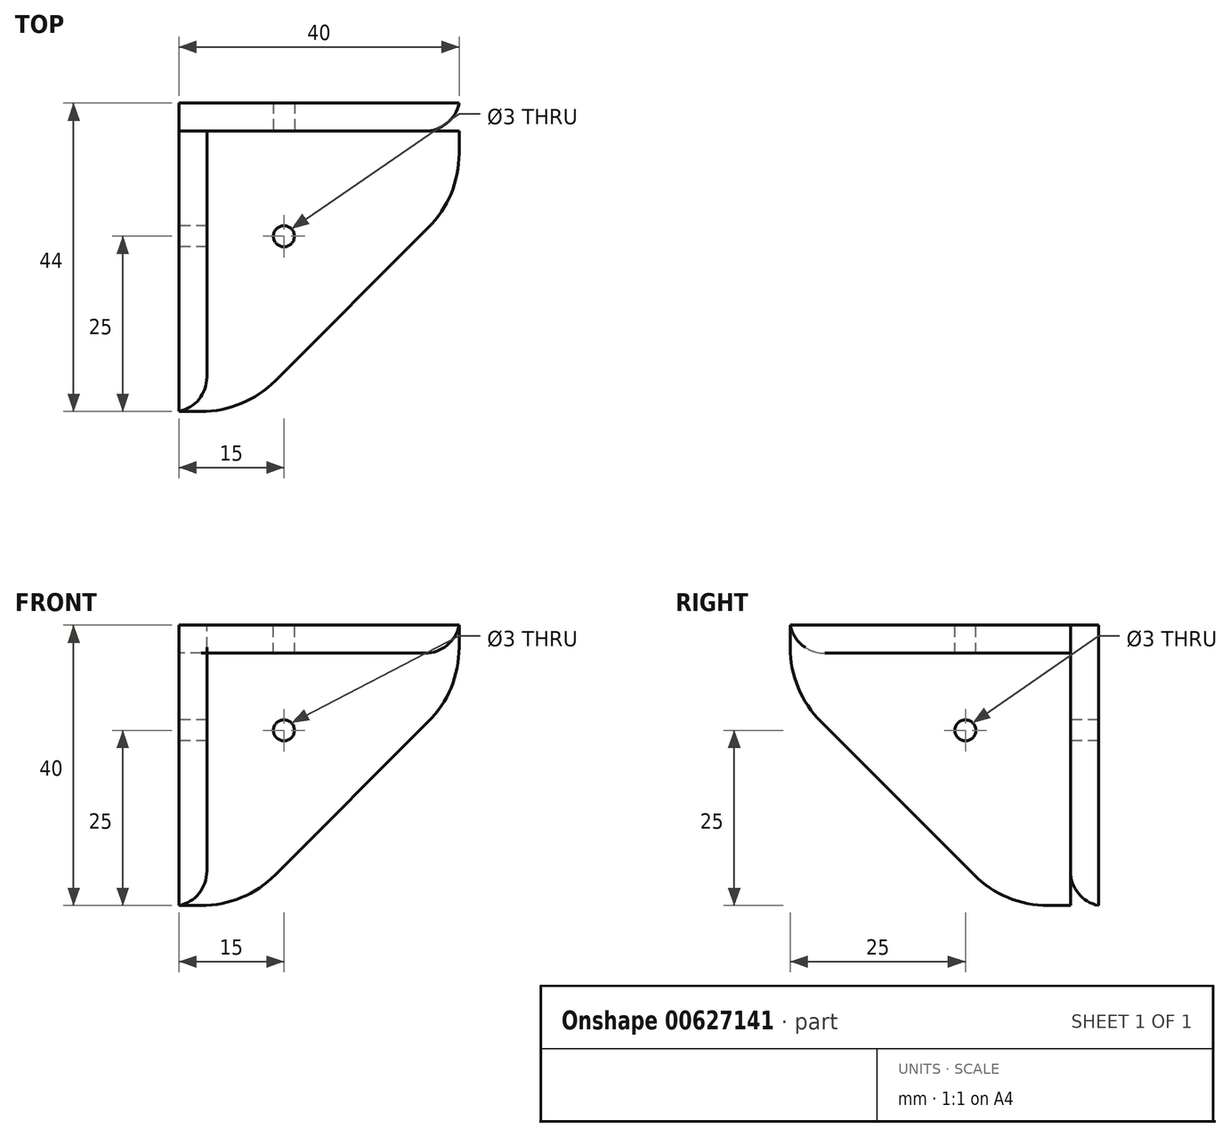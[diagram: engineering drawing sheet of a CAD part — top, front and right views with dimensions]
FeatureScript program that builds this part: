
annotation { "Feature Type Name" : "Feature", "Feature Type Description" : "" }
export const myFeature = defineFeature(function(context is Context, id is Id, definition is map)
    precondition{}
    {
        {
            var Q0;
            Q0=qCreatedBy(makeId("Front.planeOp"),FACE);
            var sketch = newSketch(context, id + "F0", { "sketchPlane" : qUnion([Q0])});
            skLineSegment(sketch, "E0.bottom", {"start": v(0, 0) * mm, "end": v(40, 0) * mm});
            skLineSegment(sketch, "E0.top", {"start": v(0, -40) * mm, "end": v(40, -40) * mm});
            skLineSegment(sketch, "E0.left", {"start": v(0, 0) * mm, "end": v(0, -40) * mm});
            skLineSegment(sketch, "E0.right", {"start": v(40, 0) * mm, "end": v(40, -40) * mm});
            skLineSegment(sketch, "E1", {"start": v(57.97, 8.58) * mm, "end": v(-37.76, -87.15) * mm});
            skPoint(sketch, "E2", {"position": v(0, -15) * mm});
            skPoint(sketch, "E3", {"position": v(15, 0) * mm});
            skCircle(sketch, "E4", {"center": v(15, -15) * mm, "radius": 1.5 * mm});
            skSolve(sketch);
        }
        {
            var Q0;
            {var subQ1=sQuery(id+"F0.wireOp",EDGE,"E0.bottom");Q0=makeQuery(id+"F0.imprint","IMPRINT",FACE,{"disambiguationData":[TD([[makeQuery(id+"F0.imprint","IMPRINT",EDGE,{"derivedFrom":subQ1}),-1.0]])]});}
            extrude(context, id + "F1", {"entities" : qUnion([Q0]), "oppositeDirection" : true, "depth" : 4 * mm, "offsetDistance" : 25 * mm});
        }
        {
            var Q0;
            Q0=makeQuery(id+"F1.opExtrude","SWEPT_EDGE",EDGE,{"disambiguationData":[OSD([sQuery(id+"F0.wireOp",EDGE,"E0.top"),sQuery(id+"F0.wireOp",EDGE,"E1")])]});
            var Q1;
            Q1=makeQuery(id+"F1.opExtrude","SWEPT_EDGE",EDGE,{"disambiguationData":[OSD([sQuery(id+"F0.wireOp",EDGE,"E0.right"),sQuery(id+"F0.wireOp",EDGE,"E1")])]});
            fillet(context, id + "F2", {"entities" : qUnion([Q0, Q1]), "radius" : 15 * mm, "tangentPropagation" : true, "allowEdgeOverflow" : false});
        }
        {
            var Q0;
            Q0=makeQuery(id+"F1.opExtrude","SWEPT_BODY",BODY,{"disambiguationData":[OSD([sQuery(id+"F0.wireOp",EDGE,"E0.bottom"),sQuery(id+"F0.wireOp",EDGE,"E0.top"),sQuery(id+"F0.wireOp",EDGE,"E0.left"),sQuery(id+"F0.wireOp",EDGE,"E0.right"),sQuery(id+"F0.wireOp",EDGE,"E1"),sQuery(id+"F0.wireOp",EDGE,"E4")])]});
            var Q1;
            Q1=makeQuery(id+"F1.opExtrude","CAP_EDGE",EDGE,{"disambiguationData":[OSD([sQuery(id+"F0.wireOp",EDGE,"E0.left")])],"isStart":true});
            transform(context, id + "F3", {"entities" : qUnion([Q0]), "transformType" : TransformType.ROTATION, "transformAxis" : qUnion([Q1]), "angle" : 90 * degree, "makeCopy" : true});
        }
        {
            var Q0;
            Q0=makeQuery(id+"F1.opExtrude","SWEPT_BODY",BODY,{"disambiguationData":[OSD([sQuery(id+"F0.wireOp",EDGE,"E0.bottom"),sQuery(id+"F0.wireOp",EDGE,"E0.top"),sQuery(id+"F0.wireOp",EDGE,"E0.left"),sQuery(id+"F0.wireOp",EDGE,"E0.right"),sQuery(id+"F0.wireOp",EDGE,"E1"),sQuery(id+"F0.wireOp",EDGE,"E4")])]});
            var Q1;
            Q1=makeQuery(id+"F1.opExtrude","CAP_EDGE",EDGE,{"disambiguationData":[OSD([sQuery(id+"F0.wireOp",EDGE,"E0.bottom")])],"isStart":true});
            transform(context, id + "F4", {"entities" : qUnion([Q0]), "transformType" : TransformType.ROTATION, "transformAxis" : qUnion([Q1]), "angle" : 270 * degree, "makeCopy" : true});
        }
        {
            var Q0;
            Q0=makeQuery(id+"F4.opPattern","COPY",EDGE,{"derivedFrom":makeQuery(id+"F1.opExtrude","CAP_EDGE",EDGE,{"disambiguationData":[OSD([sQuery(id+"F0.wireOp",EDGE,"E1")])],"isStart":false}),"instanceName":"1"});
            var Q1;
            Q1=makeQuery(id+"F1.opExtrude","CAP_EDGE",EDGE,{"disambiguationData":[OSD([sQuery(id+"F0.wireOp",EDGE,"E1")])],"isStart":true});
            var Q2;
            Q2=makeQuery(id+"F3.opPattern","COPY",EDGE,{"derivedFrom":makeQuery(id+"F1.opExtrude","CAP_EDGE",EDGE,{"disambiguationData":[OSD([sQuery(id+"F0.wireOp",EDGE,"E1")])],"isStart":false}),"instanceName":"1"});
            fillet(context, id + "F5", {"entities" : qUnion([Q0, Q1, Q2]), "radius" : 5 * mm, "tangentPropagation" : true, "allowEdgeOverflow" : false});
        }
    });
